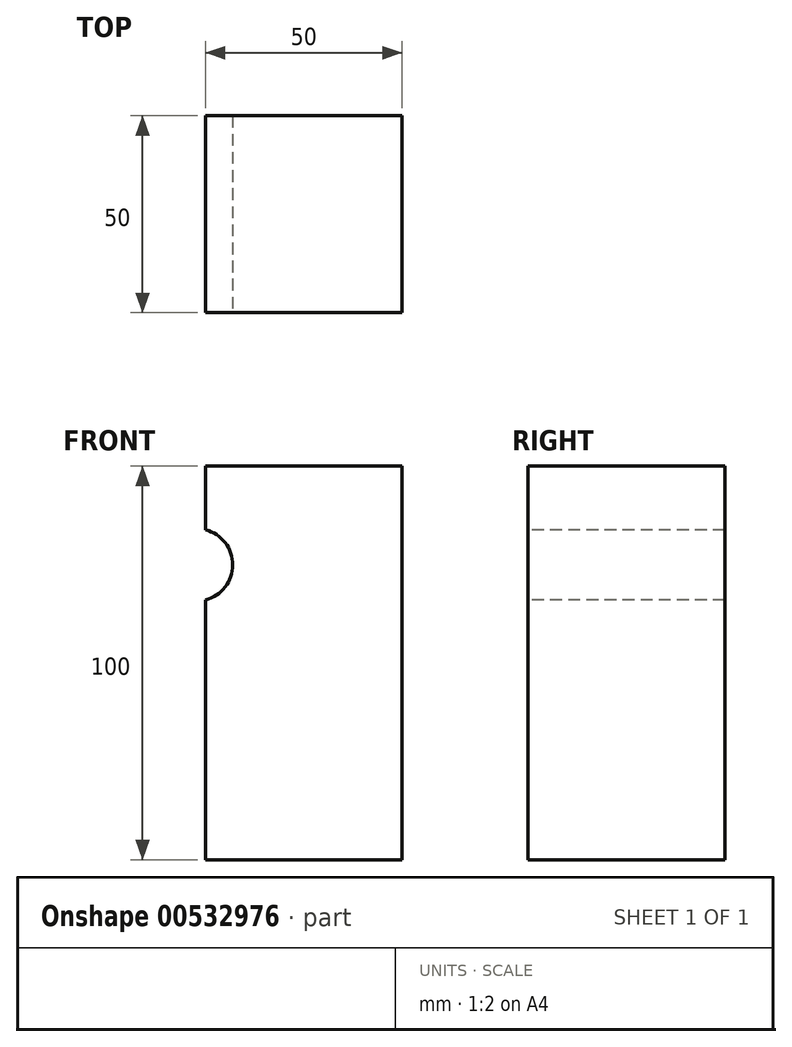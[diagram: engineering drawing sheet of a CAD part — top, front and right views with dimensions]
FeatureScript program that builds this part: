
annotation { "Feature Type Name" : "Feature", "Feature Type Description" : "" }
export const myFeature = defineFeature(function(context is Context, id is Id, definition is map)
    precondition{}
    {
        {
            var Q0;
            Q0=qCreatedBy(makeId("Top.planeOp"),FACE);
            var sketch = newSketch(context, id + "F0", { "sketchPlane" : qUnion([Q0])});
            skLineSegment(sketch, "E0.bottom", {"start": v(25, -25) * mm, "end": v(-25, -25) * mm});
            skLineSegment(sketch, "E0.top", {"start": v(25, 25) * mm, "end": v(-25, 25) * mm});
            skLineSegment(sketch, "E0.left", {"start": v(25, -25) * mm, "end": v(25, 25) * mm});
            skLineSegment(sketch, "E0.right", {"start": v(-25, -25) * mm, "end": v(-25, 25) * mm});
            skPoint(sketch, "E0.middle", {"position": v(0, 0) * mm});
            skSolve(sketch);
        }
        {
            var Q0;
            Q0=makeQuery(id+"F0.imprint","IMPRINT",FACE,{"disambiguationData":[TD([[makeQuery(id+"F0.imprint","IMPRINT",EDGE,{"derivedFrom":sQuery(id+"F0.wireOp",EDGE,"E0.bottom")}),-1.0]])]});
            extrude(context, id + "F1", {"entities" : qUnion([Q0]), "depth" : 100 * mm, "offsetDistance" : 25 * mm});
        }
        {
            var Q0;
            Q0=makeQuery(id+"F1.opExtrude","SWEPT_FACE",FACE,{"disambiguationData":[OSD([sQuery(id+"F0.wireOp",EDGE,"E0.bottom")])]});
            var sketch = newSketch(context, id + "F2", { "sketchPlane" : qUnion([Q0])});
            skCircle(sketch, "E1", {"center": v(-27.25, 74.9) * mm, "radius": 9.19 * mm});
            skSolve(sketch);
        }
        {
            var Q0;
            Q0 = qSketchRegion(id + "F2", true);
            extrude(context, id + "F3", {"entities" : qUnion([Q0]), "operationType" : NewBodyOperationType.REMOVE, "endBound" : BoundingType.THROUGH_ALL, "oppositeDirection" : true, "depth" : 25 * mm, "offsetDistance" : 25 * mm});
        }
    });
